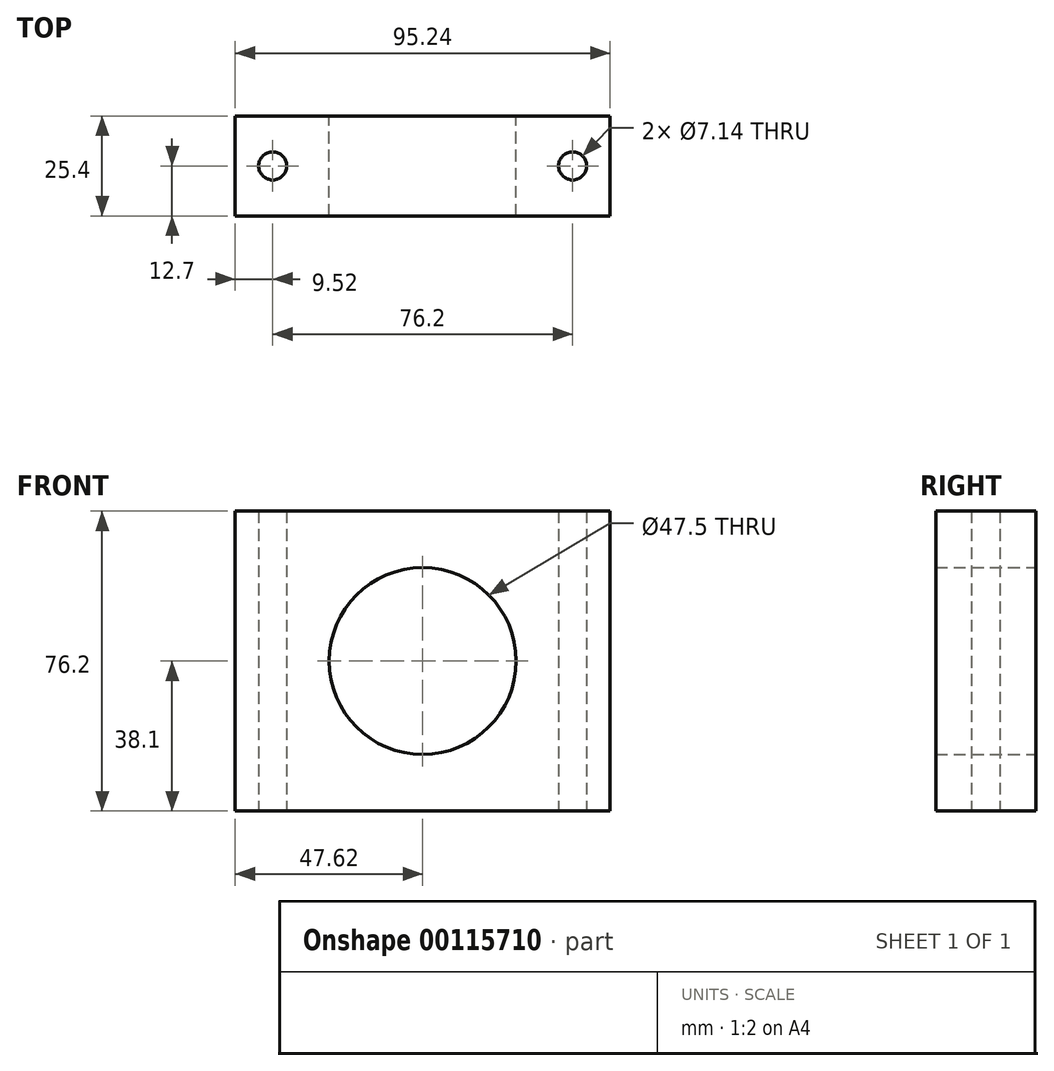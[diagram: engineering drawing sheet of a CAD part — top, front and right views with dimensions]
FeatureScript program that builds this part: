
annotation { "Feature Type Name" : "Feature", "Feature Type Description" : "" }
export const myFeature = defineFeature(function(context is Context, id is Id, definition is map)
    precondition{}
    {
        {
            var Q0;
            Q0=qCreatedBy(makeId("Top.planeOp"),FACE);
            var sketch = newSketch(context, id + "F0", { "sketchPlane" : qUnion([Q0])});
            skLineSegment(sketch, "E0", {"start": v(-47.63, 0) * mm, "end": v(47.63, 0) * mm});
            skLineSegment(sketch, "E1", {"start": v(47.63, 0) * mm, "end": v(47.63, -25.4) * mm});
            skLineSegment(sketch, "E2", {"start": v(47.63, -25.4) * mm, "end": v(-47.63, -25.4) * mm});
            skLineSegment(sketch, "E3", {"start": v(-47.63, -25.4) * mm, "end": v(-47.63, 0) * mm});
            skCircle(sketch, "E4", {"center": v(-38.1, -12.7) * mm, "radius": 3.57 * mm});
            skCircle(sketch, "E5", {"center": v(38.1, -12.7) * mm, "radius": 3.57 * mm});
            skLineSegment(sketch, "E6", {"start": v(-38.1, -12.7) * mm, "end": v(-47.63, -12.7) * mm, "construction": true});
            skLineSegment(sketch, "E7", {"start": v(38.1, -12.7) * mm, "end": v(47.63, -12.7) * mm, "construction": true});
            skSolve(sketch);
        }
        {
            var Q0;
            Q0=makeQuery(id+"F0.imprint","IMPRINT",FACE,{"disambiguationData":[TD([[makeQuery(id+"F0.imprint","IMPRINT",EDGE,{"derivedFrom":sQuery(id+"F0.wireOp",EDGE,"E0")}),-1.0]])]});
            extrude(context, id + "F1", {"entities" : qUnion([Q0]), "depth" : 76.2 * mm});
        }
        {
            var Q0;
            Q0=makeQuery(id+"F1.opExtrude","SWEPT_FACE",FACE,{"disambiguationData":[OSD([sQuery(id+"F0.wireOp",EDGE,"E0")])]});
            var sketch = newSketch(context, id + "F2", { "sketchPlane" : qUnion([Q0])});
            skPoint(sketch, "E8", {"position": v(0, 0) * mm});
            skPoint(sketch, "E9", {"position": v(47.63, 38.1) * mm});
            skCircle(sketch, "E10", {"center": v(0, 38.1) * mm, "radius": 23.75 * mm});
            skSolve(sketch);
        }
        {
            var Q0;
            Q0=makeQuery(id+"F2.imprint","IMPRINT",FACE,{"disambiguationData":[TD([[makeQuery(id+"F2.imprint","IMPRINT",EDGE,{"derivedFrom":sQuery(id+"F2.wireOp",EDGE,"E10")}),1.0]])]});
            var Q1;
            Q1=makeQuery(id+"F1.opExtrude","SWEPT_FACE",FACE,{"disambiguationData":[OSD([sQuery(id+"F0.wireOp",EDGE,"E2")])]});
            extrude(context, id + "F3", {"entities" : qUnion([Q0]), "operationType" : NewBodyOperationType.REMOVE, "endBound" : BoundingType.UP_TO_SURFACE, "oppositeDirection" : true, "endBoundEntityFace" : qUnion([Q1]), "depth" : 25.4 * mm});
        }
    });
